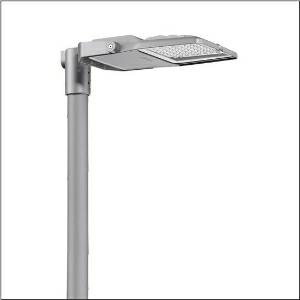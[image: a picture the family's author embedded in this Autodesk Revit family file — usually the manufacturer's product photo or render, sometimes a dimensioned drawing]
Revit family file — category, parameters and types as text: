
# Revit family: floodlight_fl_21_iq_mini___pl64_5xa7771d4e3a_aa37
name_source: partatom
category: Lighting Fixtures
units: mm (PartAtom-declared; Revit-internal decimal feet)

## family parameters
Cut with Voids When Loaded = No
Host = Face
Light Source = No
Part Type = Normal
Room Calculation Point = No
Round Connector Dimension = Use Diameter
Shared = No

## types (1)
- --- (1 x LED, 17970 lm, 143 W, 4000K)
    Apparent Load = 143 VA
    CIE Flux Codes = 28 80 98 100 100
    Color Rendering = 70
    Color Temperature = 4000K
    Default Elevation = 1800 mm
    Description = Floodlight FL 21 iQ mini, floodlight, primary light control with lens, of PMMA, primary optical cover: protective disc, of toughened safety glass, transparent, light distribution: PL64, light emission: direct distribution, installation type: surface-mounted, LED, High Power LED, rated luminous flux: 17.970lm, luminous efficacy: 126lm/W, light colour: 740, colour temperature: 4000K, control gear: iQ Comfort/DALI, control: Auto-Match, Temp-Guard, Lumen-Switch, Night-Set, Smart-Wire, Light-Fading, Desk-Remote (wireless, voltage-free reading and setting of iQ features in the workshop via application-optimized NFC function/RFID function), optimised constant luminous flux control (CLO 2.0), with terminal, 6-pole, mains connection: 220..240V, AC, 50/60Hz, start of lifetime: 143W, end of service life: 152W, reduction: 61W, luminaire housing, of diecast aluminium, powder-coated, Siteco® metallic grey (DB 702S), corrosivity category C5 mid according to DIN EN ISO 12944, suitable for swimming pools, chlorine-resistant, sealing non-destructively replaceable, please order mast flange separately, mast bracket, of steel, galvanised, powder-coated, Siteco® metallic grey (DB 702S), protection rating (complete): IP66, insulation class (complete): insulation class II (safety insulation), certification: CE, ENEC, VDE, protection symbol: D, impact resistance: IK08, permissible operating ambient temperature: -40..+40°C, permissible operating ambient temperature for outdoor applications: -40..+50°C, standard: DIN EN 12944, LABS conformity tested according to VDMA 24364:2018-05, packaging unit: 1 piece

Light Distribution: PL64
    Height = 70 mm
    Lamp = 1 x LED
    Lamp Light Flux = 17970 lm
    Lamp Power = 143 W
    Lamp count = 1
    Length = 485 mm
    Luminous efficacy = 126 lm/W
    Manufacturer = Siteco
    ModVariant = No
    Model = 5XA7771D4E3A
    Number of Poles = 1
    OnlyDefault = Yes
    Power Factor = 1
    Product Name = Floodlight FL 21 iQ mini | PL64
    Product group = floodlight | pylon annexe
    ProductGroupID = 6201
    Protection Class = Protection class II
    Protection Degree = IP 66
    RLX_Detail_Level = 1
    RLX_Emergency_Light_Flux = 0 lm
    RLX_Emergency_Type = 0
    RLX_Emergency_Type_DB = No
    RlxData = <blob elided: 101669 chars, md5=d918ac82>
    Socket = socket
    Standby Power = 0 W
    System Light Flux = 17970 lm
    System Power = 143 W
    Type Comments = factory setting: luminous flux: 100 % | dim-lin: 254 | 730 mA
    Type Image = l_1007125.jpg
    URL = http://relux.com
    VarID = @adj_187419
    Voltage = 0 V
    Weight = 0.00 kg
    Width = 337 mm

## geometry (parser evidence)
native form markers: Blend x4, Sweep x12
no freeform markers — native parametric forms only
